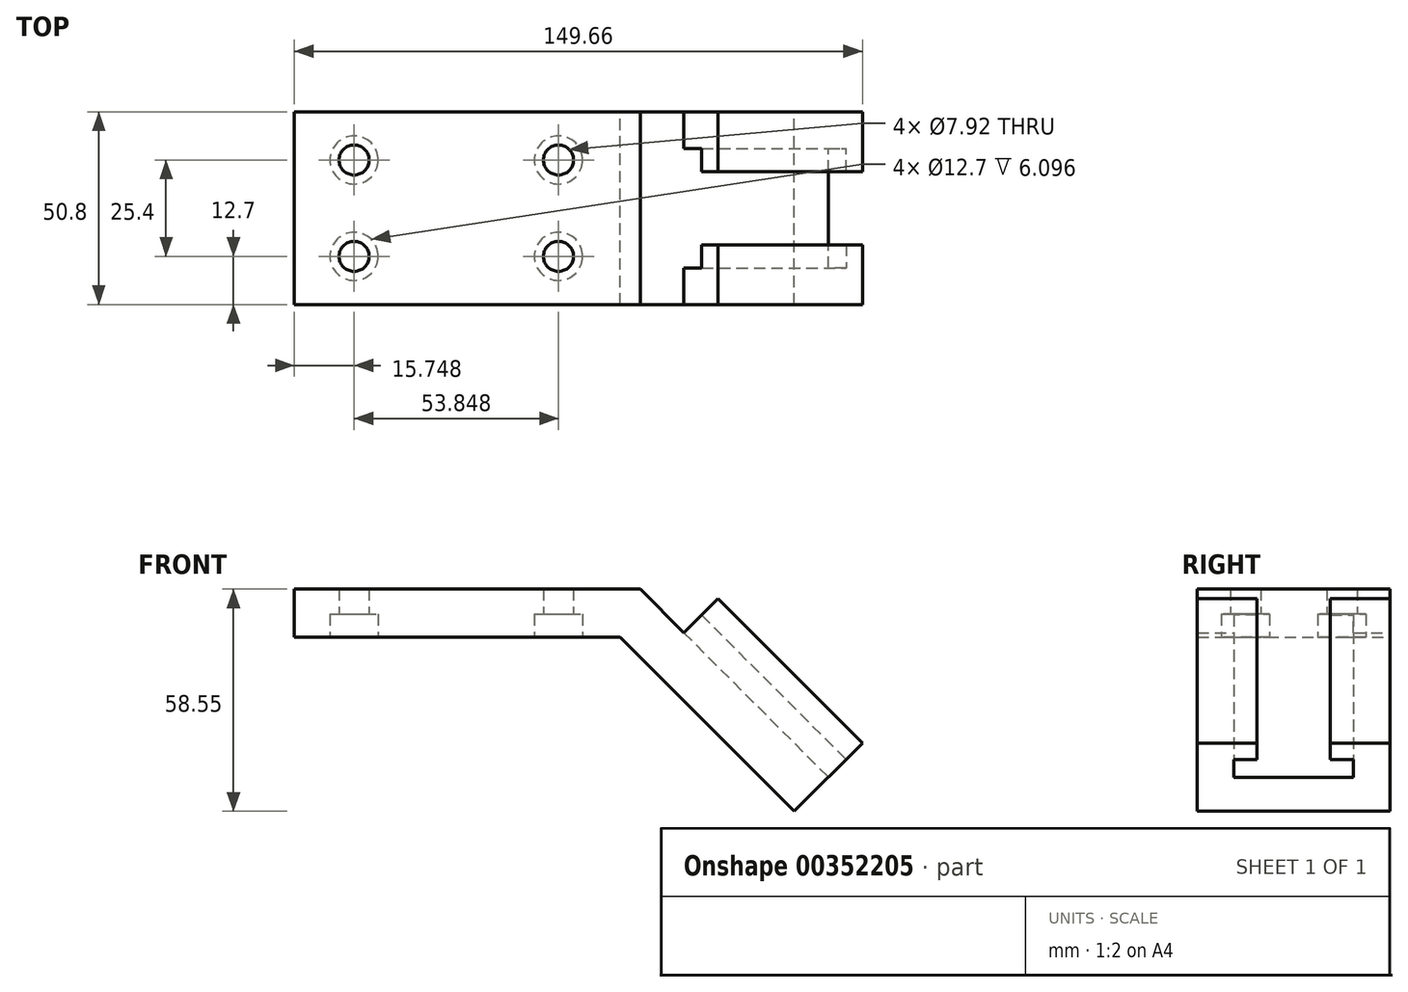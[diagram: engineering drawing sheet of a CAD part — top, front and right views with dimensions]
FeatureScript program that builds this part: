
annotation { "Feature Type Name" : "Feature", "Feature Type Description" : "" }
export const myFeature = defineFeature(function(context is Context, id is Id, definition is map)
    precondition{}
    {
        {
            var Q0;
            Q0=qCreatedBy(makeId("Front.planeOp"),FACE);
            var sketch = newSketch(context, id + "F0", { "sketchPlane" : qUnion([Q0])});
            skLineSegment(sketch, "E0", {"start": v(85.85, 0) * mm, "end": v(0, 0) * mm});
            skLineSegment(sketch, "E1", {"start": v(0, 0) * mm, "end": v(0, 12.7) * mm});
            skLineSegment(sketch, "E2", {"start": v(0, 12.7) * mm, "end": v(91.11, 12.7) * mm});
            skLineSegment(sketch, "E3", {"start": v(91.11, 12.7) * mm, "end": v(140.68, -36.87) * mm});
            skLineSegment(sketch, "E4", {"start": v(140.68, -36.87) * mm, "end": v(131.7, -45.85) * mm});
            skLineSegment(sketch, "E5", {"start": v(131.7, -45.85) * mm, "end": v(85.85, 0) * mm});
            skLineSegment(sketch, "E6", {"start": v(140.68, -36.87) * mm, "end": v(149.66, -27.9) * mm});
            skLineSegment(sketch, "E7", {"start": v(149.66, -27.9) * mm, "end": v(111.59, 10.19) * mm});
            skLineSegment(sketch, "E8", {"start": v(111.59, 10.19) * mm, "end": v(102.6, 1.2) * mm});
            skSolve(sketch);
        }
        {
            var Q0;
            Q0=makeQuery(id+"F0.imprint","IMPRINT",FACE,{"disambiguationData":[TD([[makeQuery(id+"F0.imprint","IMPRINT",EDGE,{"derivedFrom":sQuery(id+"F0.wireOp",EDGE,"E0")}),-1.0]])]});
            var Q1;
            {var subQ0=sQuery(id+"F0.wireOp",EDGE,"E6");Q1=makeQuery(id+"F0.imprint","IMPRINT",FACE,{"disambiguationData":[TD([[makeQuery(id+"F0.imprint","IMPRINT",EDGE,{"derivedFrom":subQ0}),1.0]])]});}
            extrude(context, id + "F1", {"entities" : qUnion([Q0, Q1]), "depth" : 50.8 * mm});
        }
        {
            var Q0;
            Q0=makeQuery(id+"F1.opExtrude","SWEPT_FACE",FACE,{"disambiguationData":[OSD([sQuery(id+"F0.wireOp",EDGE,"E0")])]});
            var sketch = newSketch(context, id + "F2", { "sketchPlane" : qUnion([Q0])});
            skCircle(sketch, "E9", {"center": v(15.75, 38.1) * mm, "radius": 3.96 * mm});
            skCircle(sketch, "E10", {"center": v(69.6, 38.1) * mm, "radius": 3.96 * mm});
            skCircle(sketch, "E11", {"center": v(69.6, 12.7) * mm, "radius": 3.96 * mm});
            skCircle(sketch, "E12", {"center": v(15.75, 12.7) * mm, "radius": 3.96 * mm});
            skSolve(sketch);
        }
        {
            var Q0;
            Q0=sQuery(id+"F2.wireOp",VERTEX,"E9.center");
            var Q1;
            Q1=sQuery(id+"F2.wireOp",VERTEX,"E10.center");
            var Q2;
            Q2=sQuery(id+"F2.wireOp",VERTEX,"E11.center");
            var Q3;
            Q3=sQuery(id+"F2.wireOp",VERTEX,"E12.center");
            var Q4;
            Q4=makeQuery(id+"F1.opExtrude","SWEPT_BODY",BODY,{"disambiguationData":[OSD([sQuery(id+"F0.wireOp",EDGE,"E0"),sQuery(id+"F0.wireOp",EDGE,"E1"),sQuery(id+"F0.wireOp",EDGE,"E2"),sQuery(id+"F0.wireOp",EDGE,"E3"),sQuery(id+"F0.wireOp",EDGE,"E4"),sQuery(id+"F0.wireOp",EDGE,"E5"),sQuery(id+"F0.wireOp",EDGE,"E6"),sQuery(id+"F0.wireOp",EDGE,"E7"),sQuery(id+"F0.wireOp",EDGE,"E8")])]});
            hole(context, id + "F3", {"style" : HoleStyle.C_BORE, "endStyle" : HoleEndStyle.THROUGH, "holeDiameter" : 7.92 * mm, "cBoreDiameter" : 12.7 * mm, "cBoreDepth" : 6.1 * mm, "isTappedThrough" : true, "tappedDepth" : 12.7 * mm, "tapClearance" : 3, "locations" : qUnion([Q0, Q1, Q2, Q3]), "scope" : qUnion([Q4])});
        }
        {
            var Q0;
            Q0=makeQuery(id+"F1.opExtrude","SWEPT_FACE",FACE,{"disambiguationData":[OSD([sQuery(id+"F0.wireOp",EDGE,"E4"),sQuery(id+"F0.wireOp",EDGE,"E6")])]});
            var sketch = newSketch(context, id + "F4", { "sketchPlane" : qUnion([Q0])});
            skLineSegment(sketch, "E13", {"start": v(-35.05, 86.1) * mm, "end": v(-15.75, 86.1) * mm});
            skLineSegment(sketch, "E14", {"start": v(-15.75, 86.1) * mm, "end": v(-15.75, 80.01) * mm});
            skLineSegment(sketch, "E15", {"start": v(-15.75, 80.01) * mm, "end": v(-9.65, 80.01) * mm});
            skLineSegment(sketch, "E16", {"start": v(-35.05, 86.1) * mm, "end": v(-35.05, 80.01) * mm});
            skLineSegment(sketch, "E17", {"start": v(-35.05, 80.01) * mm, "end": v(-41.15, 80.01) * mm});
            skLineSegment(sketch, "E18", {"start": v(-50.8, 73.4) * mm, "end": v(0, 73.4) * mm, "construction": true});
            skLineSegment(sketch, "E19", {"start": v(-41.15, 80.01) * mm, "end": v(-41.15, 73.4) * mm});
            skLineSegment(sketch, "E20", {"start": v(-41.15, 73.4) * mm, "end": v(-9.65, 73.4) * mm});
            skLineSegment(sketch, "E21", {"start": v(-9.65, 73.4) * mm, "end": v(-9.65, 80.01) * mm});
            skSolve(sketch);
        }
        {
            var Q0;
            Q0=makeQuery(id+"F4.imprint","IMPRINT",FACE,{"disambiguationData":[TD([[makeQuery(id+"F4.imprint","IMPRINT",EDGE,{"derivedFrom":sQuery(id+"F4.wireOp",EDGE,"E13")}),-1.0]])]});
            extrude(context, id + "F5", {"entities" : qUnion([Q0]), "operationType" : NewBodyOperationType.REMOVE, "endBound" : BoundingType.THROUGH_ALL, "oppositeDirection" : true, "depth" : 25.4 * mm});
        }
        {
            var Q0;
            {var subQ1=sQuery(id+"F0.wireOp",EDGE,"E7");Q0=makeQuery(id+"F5.boolean.opBoolean","SPLIT",FACE,{"disambiguationData":[TD([makeQuery(id+"F5.opExtrude","SWEPT_FACE",FACE,{"disambiguationData":[OSD([sQuery(id+"F4.wireOp",EDGE,"E14")])]})])],"derivedFrom":makeQuery(id+"F1.opExtrude","SWEPT_FACE",FACE,{"disambiguationData":[OSD([subQ1])]})});}
            var sketch = newSketch(context, id + "F6", { "sketchPlane" : qUnion([Q0])});
            skLineSegment(sketch, "E22", {"start": v(71.7, 0) * mm, "end": v(71.7, -50.8) * mm, "construction": true});
            skArc(sketch, "E23", {"start": v(119.18, -50.8) * mm, "mid": v(125.55, -25.4) * mm, "end": v(119.18, 0) * mm});
            skLineSegment(sketch, "E24", {"start": v(119.18, 0) * mm, "end": v(71.7, 0) * mm});
            skLineSegment(sketch, "E25", {"start": v(71.7, 0) * mm, "end": v(71.7, -50.8) * mm});
            skLineSegment(sketch, "E26", {"start": v(71.7, -50.8) * mm, "end": v(119.18, -50.8) * mm});
            skLineSegment(sketch, "E27", {"start": v(119.18, 0) * mm, "end": v(125.55, 0) * mm});
            skLineSegment(sketch, "E28", {"start": v(125.55, 0) * mm, "end": v(125.55, -50.8) * mm});
            skPoint(sketch, "E28.endSnap0", {"position": v(125.55, -25.4) * mm});
            skLineSegment(sketch, "E29", {"start": v(125.55, -50.8) * mm, "end": v(119.18, -50.8) * mm});
            skSolve(sketch);
        }
        {
            var Q0;
            {var subQ0=sQuery(id+"F6.wireOp",EDGE,"E27");Q0=makeQuery(id+"F6.imprint","IMPRINT",FACE,{"disambiguationData":[TD([[makeQuery(id+"F6.imprint","IMPRINT",EDGE,{"derivedFrom":subQ0}),1.0]])]});}
            var Q1;
            {var subQ0=sQuery(id+"F6.wireOp",EDGE,"E29");Q1=makeQuery(id+"F6.imprint","IMPRINT",FACE,{"disambiguationData":[TD([[makeQuery(id+"F6.imprint","IMPRINT",EDGE,{"derivedFrom":subQ0}),-1.0]])]});}
            var Q2;
            {var subQ0=sQuery(id+"F6.wireOp",EDGE,"E28");var subQ1=sQuery(id+"F6.wireOp",EDGE,"E23");var subQ2=makeQuery(id+"F6.imprint","INTERSECT",VERTEX,{"derivedFrom":[subQ1,subQ0]});Q2=makeQuery(id+"F6.imprint","IMPRINT",FACE,{"disambiguationData":[TD([[makeQuery(id+"F6.imprint","IMPRINT",EDGE,{"disambiguationData":[TD([[subQ2,-1.0]])],"derivedFrom":subQ1}),-1.0]])]});}
            extrude(context, id + "F7", {"entities" : qUnion([Q0, Q1, Q2]), "operationType" : NewBodyOperationType.REMOVE, "endBound" : BoundingType.THROUGH_ALL, "oppositeDirection" : true, "depth" : 25.4 * mm});
        }
    });
